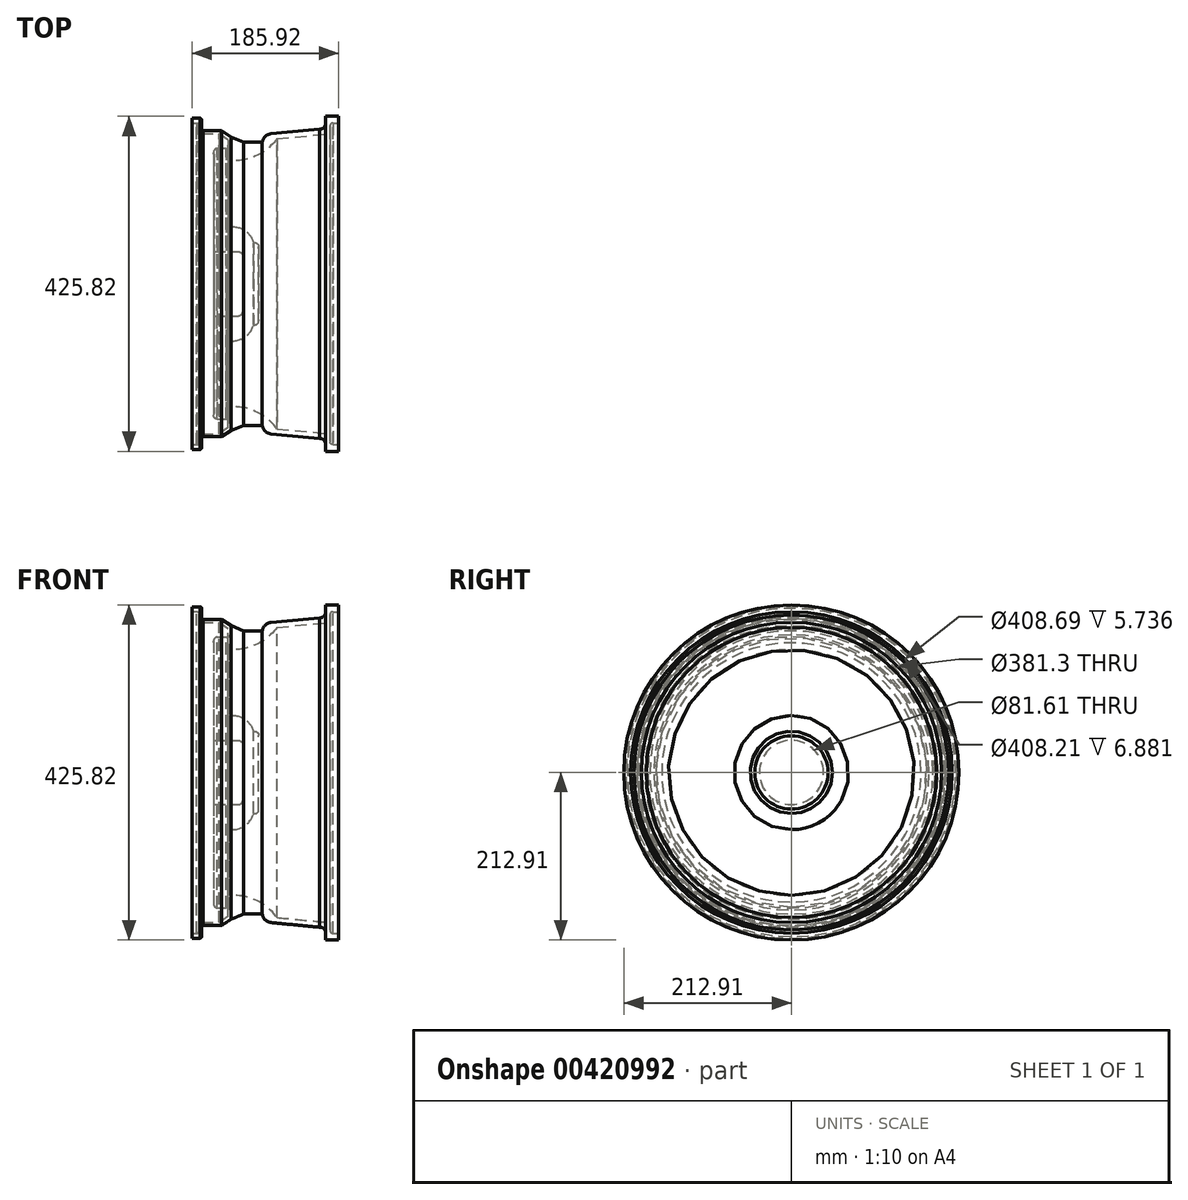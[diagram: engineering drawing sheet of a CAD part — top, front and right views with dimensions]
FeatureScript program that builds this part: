
annotation { "Feature Type Name" : "Feature", "Feature Type Description" : "" }
export const myFeature = defineFeature(function(context is Context, id is Id, definition is map)
    precondition{}
    {
        {
            var Q0;
            Q0=qCreatedBy(makeId("Front.planeOp"),FACE);
            var sketch = newSketch(context, id + "F0", { "sketchPlane" : qUnion([Q0])});
            skLineSegment(sketch, "E0", {"start": v(0, 0) * mm, "end": v(-20.13, 0) * mm});
            skLineSegment(sketch, "E1", {"start": v(-20.13, 0) * mm, "end": v(-20.13, 34.62) * mm});
            skLineSegment(sketch, "E2", {"start": v(-26.3, 40.8) * mm, "end": v(-57, 40.8) * mm});
            skLineSegment(sketch, "E3", {"start": v(-57, 40.8) * mm, "end": v(-57, 164.71) * mm});
            skLineSegment(sketch, "E4", {"start": v(0, 0) * mm, "end": v(0, 46.5) * mm});
            skLineSegment(sketch, "E5", {"start": v(-36.37, 72.5) * mm, "end": v(-36.37, 156.27) * mm});
            skArc(sketch, "E6", {"start": v(-20.13, 34.62) * mm, "mid": v(-21.94, 39) * mm, "end": v(-26.3, 40.8) * mm});
            skArc(sketch, "E7", {"start": v(0, 46.5) * mm, "mid": v(-1.73, 50.94) * mm, "end": v(-6.38, 52) * mm});
            skPoint(sketch, "E8.orphan", {"position": v(0, 52) * mm});
            skArc(sketch, "E9", {"start": v(-6.38, 52) * mm, "mid": v(-17.65, 67.69) * mm, "end": v(-36.37, 72.5) * mm});
            skLineSegment(sketch, "E10", {"start": v(-53.08, 172.08) * mm, "end": v(-41.38, 172.08) * mm});
            skLineSegment(sketch, "E11", {"start": v(-38.8, 174.9) * mm, "end": v(-38.8, 182.56) * mm});
            skLineSegment(sketch, "E12", {"start": v(-38.8, 182.56) * mm, "end": v(-50.11, 190.65) * mm});
            skLineSegment(sketch, "E13", {"start": v(-50.11, 190.65) * mm, "end": v(-72.88, 190.65) * mm});
            skLineSegment(sketch, "E14", {"start": v(-76.04, 193.82) * mm, "end": v(-76.04, 200.44) * mm});
            skLineSegment(sketch, "E15", {"start": v(-78.72, 204.35) * mm, "end": v(-84.61, 204.35) * mm});
            skLineSegment(sketch, "E16", {"start": v(-84.61, 204.35) * mm, "end": v(-84.61, 210.47) * mm});
            skLineSegment(sketch, "E17", {"start": v(-84.61, 210.47) * mm, "end": v(-74.58, 210.47) * mm});
            skLineSegment(sketch, "E18", {"start": v(-72.62, 208.5) * mm, "end": v(-72.62, 196.04) * mm});
            skLineSegment(sketch, "E19", {"start": v(-70.73, 194.32) * mm, "end": v(-46.93, 194.32) * mm});
            skLineSegment(sketch, "E20", {"start": v(-46.93, 194.32) * mm, "end": v(-35.19, 186.49) * mm});
            skLineSegment(sketch, "E21", {"start": v(-35.19, 186.49) * mm, "end": v(-19.29, 179.88) * mm});
            skLineSegment(sketch, "E22", {"start": v(-19.29, 179.88) * mm, "end": v(4.44, 179.88) * mm});
            skLineSegment(sketch, "E23", {"start": v(15.7, 190.65) * mm, "end": v(63.15, 195.3) * mm});
            skLineSegment(sketch, "E24", {"start": v(63.15, 195.3) * mm, "end": v(80, 196.83) * mm});
            skLineSegment(sketch, "E25", {"start": v(84.68, 202.84) * mm, "end": v(84.68, 212.9) * mm});
            skLineSegment(sketch, "E26", {"start": v(84.68, 212.9) * mm, "end": v(101.31, 212.9) * mm});
            skLineSegment(sketch, "E27", {"start": v(101.31, 212.9) * mm, "end": v(101.31, 204.1) * mm});
            skLineSegment(sketch, "E28", {"start": v(101.31, 204.1) * mm, "end": v(93.2, 204.1) * mm});
            skLineSegment(sketch, "E29", {"start": v(90.55, 201.6) * mm, "end": v(90.55, 190.65) * mm});
            skLineSegment(sketch, "E30", {"start": v(90.55, 190.65) * mm, "end": v(23.03, 184.29) * mm});
            skArc(sketch, "E31", {"start": v(-53.08, 172.08) * mm, "mid": v(-56.77, 169.31) * mm, "end": v(-57, 164.71) * mm});
            skPoint(sketch, "E32.orphan", {"position": v(-67.37, 172.08) * mm});
            skArc(sketch, "E33", {"start": v(-41.38, 172.08) * mm, "mid": v(-38.67, 172.2) * mm, "end": v(-38.8, 174.9) * mm});
            skPoint(sketch, "E34.orphan", {"position": v(-38.8, 172.08) * mm});
            skArc(sketch, "E35", {"start": v(-76.04, 194.4) * mm, "mid": v(-75.24, 191.87) * mm, "end": v(-72.88, 190.65) * mm});
            skPoint(sketch, "E36.orphan", {"position": v(-76.04, 190.65) * mm});
            skArc(sketch, "E37", {"start": v(-76.04, 200.44) * mm, "mid": v(-76.43, 203.14) * mm, "end": v(-78.88, 204.35) * mm});
            skArc(sketch, "E38", {"start": v(-72.62, 208.13) * mm, "mid": v(-73.25, 209.85) * mm, "end": v(-74.97, 210.47) * mm});
            skArc(sketch, "E39", {"start": v(-72.62, 196.67) * mm, "mid": v(-72.2, 195.08) * mm, "end": v(-70.73, 194.32) * mm});
            skArc(sketch, "E40", {"start": v(15.7, 190.65) * mm, "mid": v(8.2, 187.21) * mm, "end": v(4.44, 179.88) * mm});
            skArc(sketch, "E41", {"start": v(77.2, 196.57) * mm, "mid": v(82.3, 198.08) * mm, "end": v(84.68, 202.84) * mm});
            skArc(sketch, "E42", {"start": v(94.43, 204.1) * mm, "mid": v(91.36, 203.1) * mm, "end": v(90.55, 199.97) * mm});
            skArc(sketch, "E43", {"start": v(-36.37, 156.27) * mm, "mid": v(-3.07, 162.64) * mm, "end": v(23.03, 184.29) * mm});
            skSolve(sketch);
        }
        {
            var Q0;
            Q0=makeQuery(id+"F0.imprint","IMPRINT",FACE,{"disambiguationData":[TD([[makeQuery(id+"F0.imprint","IMPRINT",EDGE,{"derivedFrom":sQuery(id+"F0.wireOp",EDGE,"E0")}),-1.0]])]});
            var Q1;
            Q1=sQuery(id+"F0.wireOp",EDGE,"E0");
            revolve(context, id + "F1", {"entities" : qUnion([Q0]), "axis" : qUnion([Q1]), "revolveType" : RevolveType.FULL});
        }
    });
